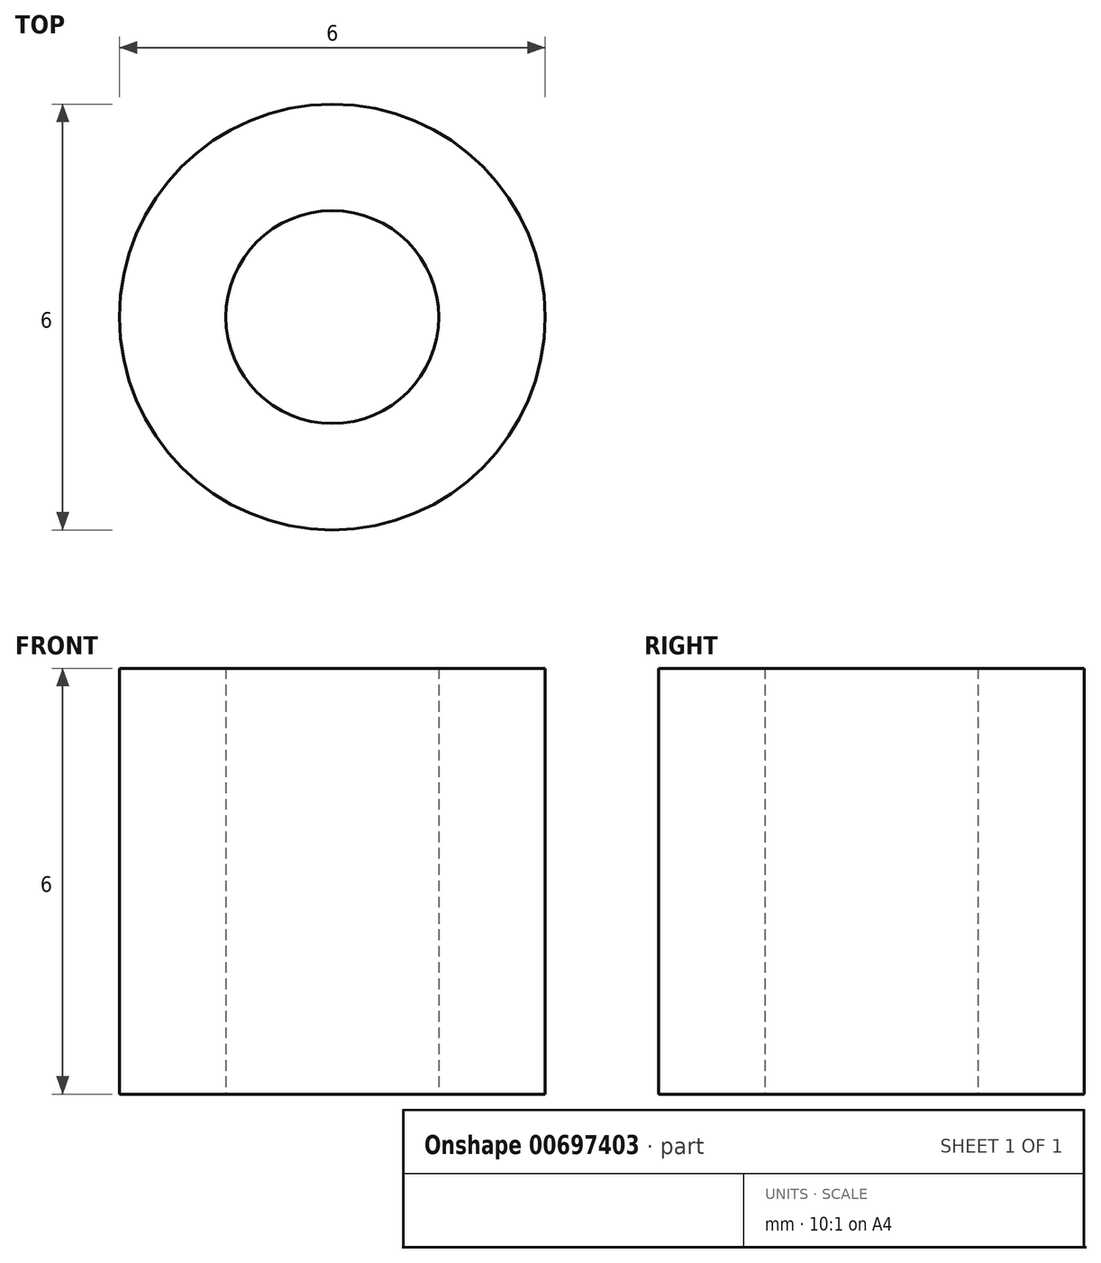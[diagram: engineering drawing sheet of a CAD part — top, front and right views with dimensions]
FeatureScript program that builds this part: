
annotation { "Feature Type Name" : "Feature", "Feature Type Description" : "" }
export const myFeature = defineFeature(function(context is Context, id is Id, definition is map)
    precondition{}
    {
        {
            var Q0;
            Q0=qCreatedBy(makeId("Top.planeOp"),FACE);
            var sketch = newSketch(context, id + "F0", { "sketchPlane" : qUnion([Q0])});
            skCircle(sketch, "E0", {"center": v(0, 0) * mm, "radius": 1.5 * mm});
            skCircle(sketch, "E1", {"center": v(0, 0) * mm, "radius": 3 * mm});
            skSolve(sketch);
        }
        {
            var Q0;
            Q0=makeQuery(id+"F0.imprint","IMPRINT",FACE,{"disambiguationData":[TD([[makeQuery(id+"F0.imprint","IMPRINT",EDGE,{"derivedFrom":sQuery(id+"F0.wireOp",EDGE,"E0")}),-1.0]])]});
            extrude(context, id + "F1", {"entities" : qUnion([Q0]), "depth" : 6 * mm, "offsetDistance" : 25 * mm});
        }
    });
